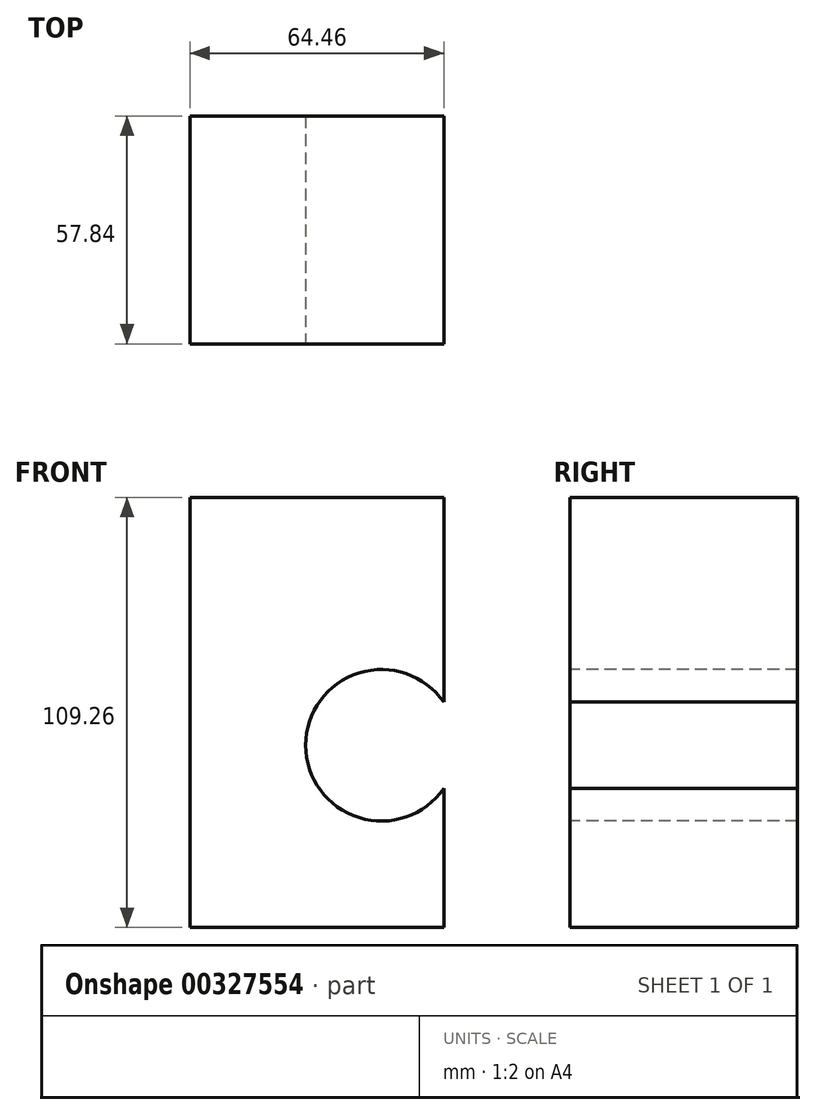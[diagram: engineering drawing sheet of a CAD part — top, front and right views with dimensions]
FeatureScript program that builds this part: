
annotation { "Feature Type Name" : "Feature", "Feature Type Description" : "" }
export const myFeature = defineFeature(function(context is Context, id is Id, definition is map)
    precondition{}
    {
        {
            var Q0;
            Q0=qCreatedBy(makeId("Top.planeOp"),FACE);
            var sketch = newSketch(context, id + "F0", { "sketchPlane" : qUnion([Q0])});
            skLineSegment(sketch, "E0.bottom", {"start": v(15.83, 0) * mm, "end": v(-48.63, 0) * mm});
            skLineSegment(sketch, "E0.top", {"start": v(15.83, 57.84) * mm, "end": v(-48.63, 57.84) * mm});
            skLineSegment(sketch, "E0.left", {"start": v(15.83, 0) * mm, "end": v(15.83, 57.84) * mm});
            skLineSegment(sketch, "E0.right", {"start": v(-48.63, 0) * mm, "end": v(-48.63, 57.84) * mm});
            skSolve(sketch);
        }
        {
            var Q0;
            Q0=makeQuery(id+"F0.imprint","IMPRINT",FACE,{"disambiguationData":[TD([[makeQuery(id+"F0.imprint","IMPRINT",EDGE,{"derivedFrom":sQuery(id+"F0.wireOp",EDGE,"E0.bottom")}),-1.0]])]});
            var sketch = newSketch(context, id + "F1", { "sketchPlane" : qUnion([Q0])});
            skSolve(sketch);
        }
        {
            var Q0;
            Q0 = qSketchRegion(id + "F1", true);
            var Q1;
            Q1=makeQuery(id+"F0.imprint","IMPRINT",FACE,{"disambiguationData":[TD([[makeQuery(id+"F0.imprint","IMPRINT",EDGE,{"derivedFrom":sQuery(id+"F0.wireOp",EDGE,"E0.bottom")}),-1.0]])]});
            extrude(context, id + "F2", {"entities" : qUnion([Q0, Q1]), "depth" : 109.26 * mm});
        }
        {
            var Q0;
            Q0=makeQuery(id+"F2.opExtrude","SWEPT_FACE",FACE,{"disambiguationData":[OSD([sQuery(id+"F0.wireOp",EDGE,"E0.bottom")])]});
            var sketch = newSketch(context, id + "F3", { "sketchPlane" : qUnion([Q0])});
            skCircle(sketch, "E1", {"center": v(0, 46.26) * mm, "radius": 19.25 * mm});
            skSolve(sketch);
        }
        {
            var Q0;
            {var subQ0=sQuery(id+"F3.wireOp",EDGE,"E1");var subQ1=makeQuery(id+"F2.opExtrude","SWEPT_EDGE",EDGE,{"disambiguationData":[OSD([sQuery(id+"F0.wireOp",EDGE,"E0.bottom"),sQuery(id+"F0.wireOp",EDGE,"E0.left")])]});var subQ2=makeQuery(id+"F3.imprint","INTERSECT",VERTEX,{"disambiguationData":[OD(0.0)],"derivedFrom":[subQ1,subQ0]});Q0=makeQuery(id+"F3.imprint","IMPRINT",FACE,{"disambiguationData":[TD([[makeQuery(id+"F3.imprint","IMPRINT",EDGE,{"disambiguationData":[TD([[subQ2,1.0]])],"derivedFrom":subQ0}),1.0]])]});}
            extrude(context, id + "F4", {"entities" : qUnion([Q0]), "operationType" : NewBodyOperationType.REMOVE, "oppositeDirection" : true, "depth" : 25.4 * mm});
        }
        {
            var Q0;
            Q0=makeQuery(id+"F2.opExtrude","SWEPT_FACE",FACE,{"disambiguationData":[OSD([sQuery(id+"F0.wireOp",EDGE,"E0.bottom")])]});
            var sketch = newSketch(context, id + "F5", { "sketchPlane" : qUnion([Q0])});
            skLineSegment(sketch, "E2.0.0", {"start": v(15.83, 35.3) * mm, "end": v(15.83, 57.21) * mm});
            skArc(sketch, "E2.0.1", {"start": v(15.83, 57.21) * mm, "mid": v(-19.25, 46.26) * mm, "end": v(15.83, 35.3) * mm});
            skSolve(sketch);
        }
        {
            var Q0;
            Q0=makeQuery(id+"F5.imprint","IMPRINT",FACE,{"disambiguationData":[TD([[makeQuery(id+"F5.imprint","IMPRINT",EDGE,{"derivedFrom":sQuery(id+"F5.wireOp",EDGE,"E2.0.0")}),1.0]])]});
            extrude(context, id + "F6", {"entities" : qUnion([Q0]), "operationType" : NewBodyOperationType.REMOVE, "oppositeDirection" : true, "depth" : 80.1 * mm});
        }
    });
